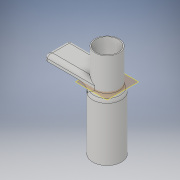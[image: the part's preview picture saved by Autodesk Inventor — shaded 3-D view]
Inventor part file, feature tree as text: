
AUTODESK INVENTOR PART (.ipt)
format: ipt  version: 2019 (Build 230136000, 136)  size: 201,728 bytes
history: native  units: mm
features: extrude x4, fillet x4, sketch x4, plane x1
ambient origin geometry x8: Origin, YZ Plane, XZ Plane, XY Plane, X Axis, Y Axis, Z Axis, Center Point
bodies: Solid1 (feature_tree)
feature tree (13):
  extrude  "Extrusion1"  Depth=23.0mm
  extrude  "Extrusion2"  Depth=19.5mm
  extrude  "Extrusion3"  Depth=5.0mm TaperAngle=0.0deg
  fillet  "Fillet1"  Radius=5.0mm
  fillet  "Fillet2"  Radius=5.0mm
  plane  "Work Plane1"
  extrude  "Extrusion4"  Depth=40.0mm
  fillet  "Fillet3"  Radius=2.0mm
  fillet  "Fillet4"  Radius=5.0mm
  sketch  "Sketch1"  dims[d0=20.0mm d1=23.0mm]
  sketch  "Sketch2"  dims[d2=40.0mm d3=0.0mm d4=19.5mm]
  sketch  "Sketch3"  dims[d5=35.0mm d6=0.0mm d7=5.0mm d8=0.0mm d9=5.0mm d10=5.0mm]
  sketch  "Sketch4"  dims[d11=50.0mm d13=40.0mm d14=2.0mm d15=5.0mm d16=0.0mm d17=5.0mm d18=3.0mm]
